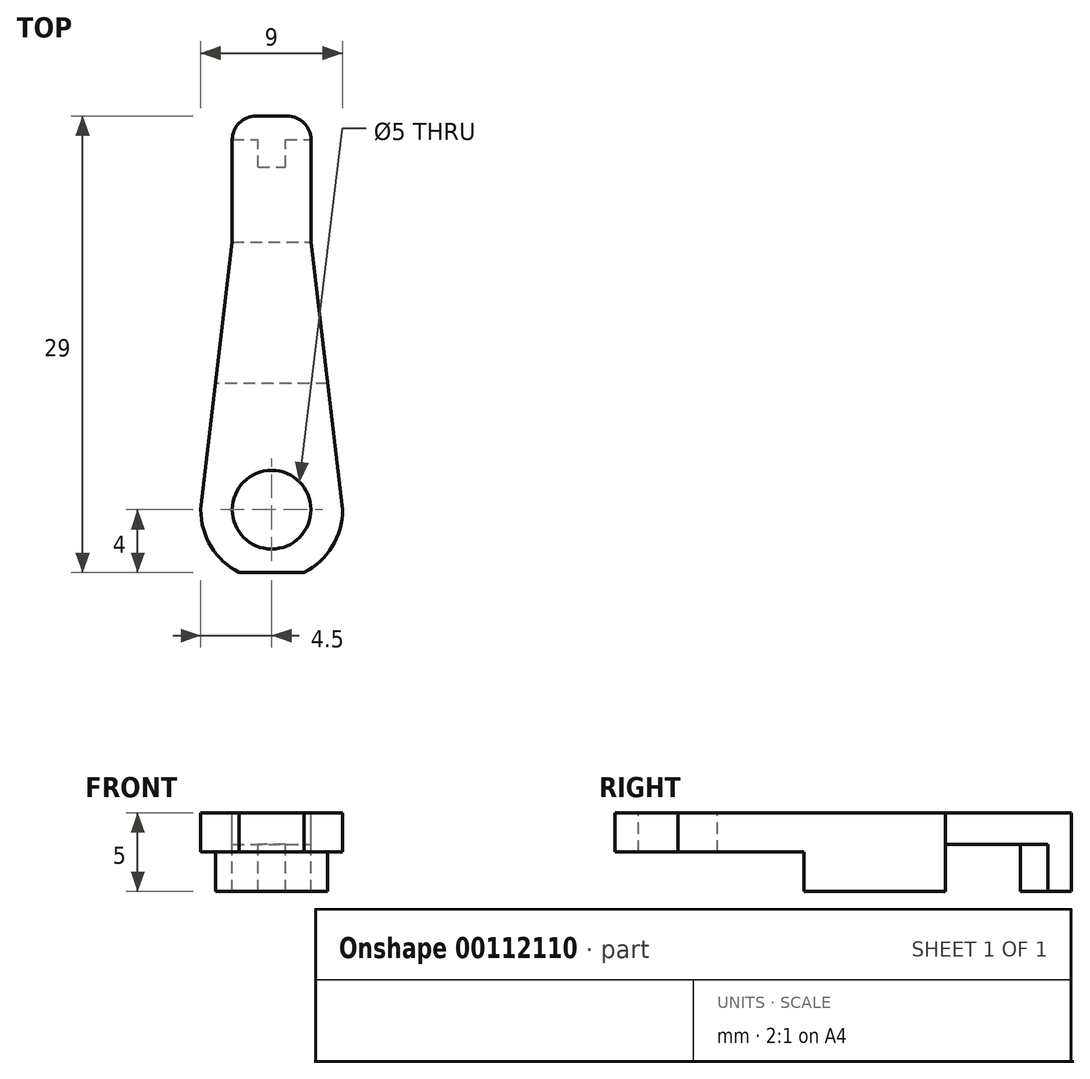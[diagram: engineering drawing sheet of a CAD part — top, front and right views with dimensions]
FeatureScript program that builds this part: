
annotation { "Feature Type Name" : "Feature", "Feature Type Description" : "" }
export const myFeature = defineFeature(function(context is Context, id is Id, definition is map)
    precondition{}
    {
        {
            var Q0;
            Q0=qCreatedBy(makeId("Top.planeOp"),FACE);
            var sketch = newSketch(context, id + "F0", { "sketchPlane" : qUnion([Q0])});
            skLineSegment(sketch, "E0.bottom", {"start": v(0, 0) * mm, "end": v(9, 0) * mm});
            skLineSegment(sketch, "E0.top", {"start": v(3.5, 29) * mm, "end": v(5.5, 29) * mm});
            skLineSegment(sketch, "E0.left", {"start": v(0, 0) * mm, "end": v(0, 29) * mm});
            skLineSegment(sketch, "E0.right", {"start": v(9, 0) * mm, "end": v(9, 27) * mm});
            skCircle(sketch, "E1", {"center": v(4.5, 4) * mm, "radius": 2.5 * mm});
            skPoint(sketch, "E1.centerSnap0", {"position": v(4.5, 0) * mm});
            skArc(sketch, "E2", {"start": v(6.56, 0) * mm, "mid": v(8.34, 1.66) * mm, "end": v(9, 4) * mm});
            skArc(sketch, "E3.trimOffspring", {"start": v(0, 4) * mm, "mid": v(0.66, 1.66) * mm, "end": v(2.44, 0) * mm});
            skLineSegment(sketch, "E4", {"start": v(0, 4) * mm, "end": v(2, 21) * mm});
            skLineSegment(sketch, "E5", {"start": v(2, 21) * mm, "end": v(0, 21) * mm});
            skLineSegment(sketch, "E6", {"start": v(9, 4) * mm, "end": v(7, 21) * mm});
            skLineSegment(sketch, "E7", {"start": v(7, 21) * mm, "end": v(9, 21) * mm});
            skLineSegment(sketch, "E8", {"start": v(2, 21) * mm, "end": v(2, 27.5) * mm});
            skLineSegment(sketch, "E9", {"start": v(7, 21) * mm, "end": v(7, 27.5) * mm});
            skArc(sketch, "E10.filletArc", {"start": v(3.5, 29) * mm, "mid": v(2.44, 28.56) * mm, "end": v(2, 27.5) * mm});
            skArc(sketch, "E11.filletArc", {"start": v(7, 27.5) * mm, "mid": v(6.56, 28.56) * mm, "end": v(5.5, 29) * mm});
            skSolve(sketch);
        }
        {
            var Q0;
            {var subQ2=sQuery(id+"F0.wireOp",EDGE,"E0.top");Q0=makeQuery(id+"F0.imprint","IMPRINT",FACE,{"disambiguationData":[TD([[makeQuery(id+"F0.imprint","IMPRINT",EDGE,{"derivedFrom":subQ2}),-1.0]])]});}
            extrude(context, id + "F1", {"entities" : qUnion([Q0]), "oppositeDirection" : true, "depth" : 5 * mm});
        }
        {
            var Q0;
            Q0=makeQuery(id+"F1.opExtrude","SWEPT_FACE",FACE,{"disambiguationData":[OSD([sQuery(id+"F0.wireOp",EDGE,"E9")])]});
            var sketch = newSketch(context, id + "F2", { "sketchPlane" : qUnion([Q0])});
            skPoint(sketch, "E12.0", {"position": v(21, 0) * mm});
            skPoint(sketch, "E13.0", {"position": v(21, -5) * mm});
            skPoint(sketch, "E14.0", {"position": v(27.5, 0) * mm});
            skPoint(sketch, "E15.0", {"position": v(27.5, -5) * mm});
            skLineSegment(sketch, "E16.bottom", {"start": v(27.5, -5) * mm, "end": v(21, -5) * mm});
            skLineSegment(sketch, "E16.top", {"start": v(27.5, -2) * mm, "end": v(21, -2) * mm});
            skLineSegment(sketch, "E16.left", {"start": v(27.5, -5) * mm, "end": v(27.5, -2) * mm});
            skLineSegment(sketch, "E16.right", {"start": v(21, -5) * mm, "end": v(21, -2) * mm});
            skLineSegment(sketch, "E17", {"start": v(27.5, -2) * mm, "end": v(27.5, -2) * mm});
            skLineSegment(sketch, "E18", {"start": v(27.5, -2) * mm, "end": v(27.5, -5) * mm});
            skLineSegment(sketch, "E19", {"start": v(27.5, -5) * mm, "end": v(27.5, -5) * mm});
            skSolve(sketch);
        }
        {
            var Q0;
            Q0=makeQuery(id+"F2.imprint","IMPRINT",FACE,{"disambiguationData":[TD([[makeQuery(id+"F2.imprint","IMPRINT",EDGE,{"derivedFrom":sQuery(id+"F2.wireOp",EDGE,"E16.bottom")}),1.0]])]});
            extrude(context, id + "F3", {"entities" : qUnion([Q0]), "operationType" : NewBodyOperationType.REMOVE, "oppositeDirection" : true, "depth" : 25 * mm});
        }
        {
            var Q0;
            Q0=makeQuery(id+"F3.boolean.opBoolean","COPY",FACE,{"derivedFrom":makeQuery(id+"F3.opExtrude","SWEPT_FACE",FACE,{"disambiguationData":[OSD([sQuery(id+"F2.wireOp",EDGE,"E16.top")])]})});
            var sketch = newSketch(context, id + "F4", { "sketchPlane" : qUnion([Q0])});
            skLineSegment(sketch, "E20.bottom", {"start": v(5.37, -27.5) * mm, "end": v(3.62, -27.5) * mm});
            skLineSegment(sketch, "E20.top", {"start": v(5.37, -25.75) * mm, "end": v(3.62, -25.75) * mm});
            skLineSegment(sketch, "E20.left", {"start": v(5.37, -27.5) * mm, "end": v(5.37, -25.75) * mm});
            skLineSegment(sketch, "E20.right", {"start": v(3.62, -27.5) * mm, "end": v(3.62, -25.75) * mm});
            skPoint(sketch, "E20.middle", {"position": v(4.5, -26.62) * mm});
            skPoint(sketch, "E20.middle.positionSnap0", {"position": v(4.5, -27.5) * mm});
            skPoint(sketch, "E20.centerSnap0", {"position": v(4.5, -27.5) * mm});
            skSolve(sketch);
        }
        {
            var Q0;
            Q0=makeQuery(id+"F4.imprint","IMPRINT",FACE,{"disambiguationData":[TD([[makeQuery(id+"F4.imprint","IMPRINT",EDGE,{"derivedFrom":sQuery(id+"F4.wireOp",EDGE,"E20.bottom")}),1.0]])]});
            var Q1;
            {var subQ0=sQuery(id+"F0.wireOp",EDGE,"E0.top");var subQ1=sQuery(id+"F0.wireOp",EDGE,"E10.filletArc");var subQ2=sQuery(id+"F0.wireOp",EDGE,"E11.filletArc");Q1=makeQuery(id+"F3.boolean.opBoolean","SPLIT",FACE,{"disambiguationData":[TD([makeQuery(id+"F1.opExtrude","SWEPT_FACE",FACE,{"disambiguationData":[OSD([subQ0])]})])],"derivedFrom":makeQuery(id+"F1.opExtrude","CAP_FACE",FACE,{"disambiguationData":[OSD([sQuery(id+"F0.wireOp",EDGE,"E0.bottom"),subQ0,sQuery(id+"F0.wireOp",EDGE,"E1"),sQuery(id+"F0.wireOp",EDGE,"E2"),sQuery(id+"F0.wireOp",EDGE,"E3.trimOffspring"),sQuery(id+"F0.wireOp",EDGE,"E4"),sQuery(id+"F0.wireOp",EDGE,"E6"),sQuery(id+"F0.wireOp",EDGE,"E8"),sQuery(id+"F0.wireOp",EDGE,"E9"),subQ1,subQ2])],"isStart":false})});}
            extrude(context, id + "F5", {"entities" : qUnion([Q0]), "operationType" : NewBodyOperationType.ADD, "endBound" : BoundingType.UP_TO_SURFACE, "endBoundEntityFace" : qUnion([Q1]), "depth" : 25 * mm});
        }
        {
            var Q0;
            {var subQ0=sQuery(id+"F0.wireOp",EDGE,"E3.trimOffspring");var subQ1=sQuery(id+"F0.wireOp",EDGE,"E2");var subQ2=sQuery(id+"F0.wireOp",EDGE,"E1");var subQ3=sQuery(id+"F0.wireOp",EDGE,"E0.bottom");var subQ4=sQuery(id+"F0.wireOp",EDGE,"E4");var subQ5=sQuery(id+"F0.wireOp",EDGE,"E6");Q0=makeQuery(id+"F3.boolean.opBoolean","SPLIT",FACE,{"disambiguationData":[TD([makeQuery(id+"F1.opExtrude","SWEPT_FACE",FACE,{"disambiguationData":[OSD([subQ3])]})])],"derivedFrom":makeQuery(id+"F1.opExtrude","CAP_FACE",FACE,{"disambiguationData":[OSD([subQ3,sQuery(id+"F0.wireOp",EDGE,"E0.top"),subQ2,subQ1,subQ0,subQ4,subQ5,sQuery(id+"F0.wireOp",EDGE,"E8"),sQuery(id+"F0.wireOp",EDGE,"E9"),sQuery(id+"F0.wireOp",EDGE,"E10.filletArc"),sQuery(id+"F0.wireOp",EDGE,"E11.filletArc")])],"isStart":false})});}
            var sketch = newSketch(context, id + "F6", { "sketchPlane" : qUnion([Q0])});
            skLineSegment(sketch, "E21.0.0", {"start": v(0, -4) * mm, "end": v(2, -21) * mm});
            skLineSegment(sketch, "E21.0.1", {"start": v(2, -21) * mm, "end": v(7, -21) * mm});
            skLineSegment(sketch, "E21.0.2", {"start": v(7, -21) * mm, "end": v(9, -4) * mm});
            skArc(sketch, "E21.0.3", {"start": v(9, -4) * mm, "mid": v(8.34, -1.66) * mm, "end": v(6.56, 0) * mm});
            skLineSegment(sketch, "E21.0.4", {"start": v(6.56, 0) * mm, "end": v(2.44, 0) * mm});
            skArc(sketch, "E21.0.5", {"start": v(2.44, 0) * mm, "mid": v(0.66, -1.66) * mm, "end": v(0, -4) * mm});
            skLineSegment(sketch, "E22", {"start": v(8.06, -12) * mm, "end": v(0.94, -12) * mm});
            skSolve(sketch);
        }
        {
            var Q0;
            {var subQ0=sQuery(id+"F6.wireOp",EDGE,"E21.0.3");Q0=makeQuery(id+"F6.imprint","IMPRINT",FACE,{"disambiguationData":[TD([[makeQuery(id+"F6.imprint","IMPRINT",EDGE,{"derivedFrom":subQ0}),-1.0]])]});}
            extrude(context, id + "F7", {"entities" : qUnion([Q0]), "operationType" : NewBodyOperationType.REMOVE, "oppositeDirection" : true, "depth" : 2.5 * mm});
        }
    });
